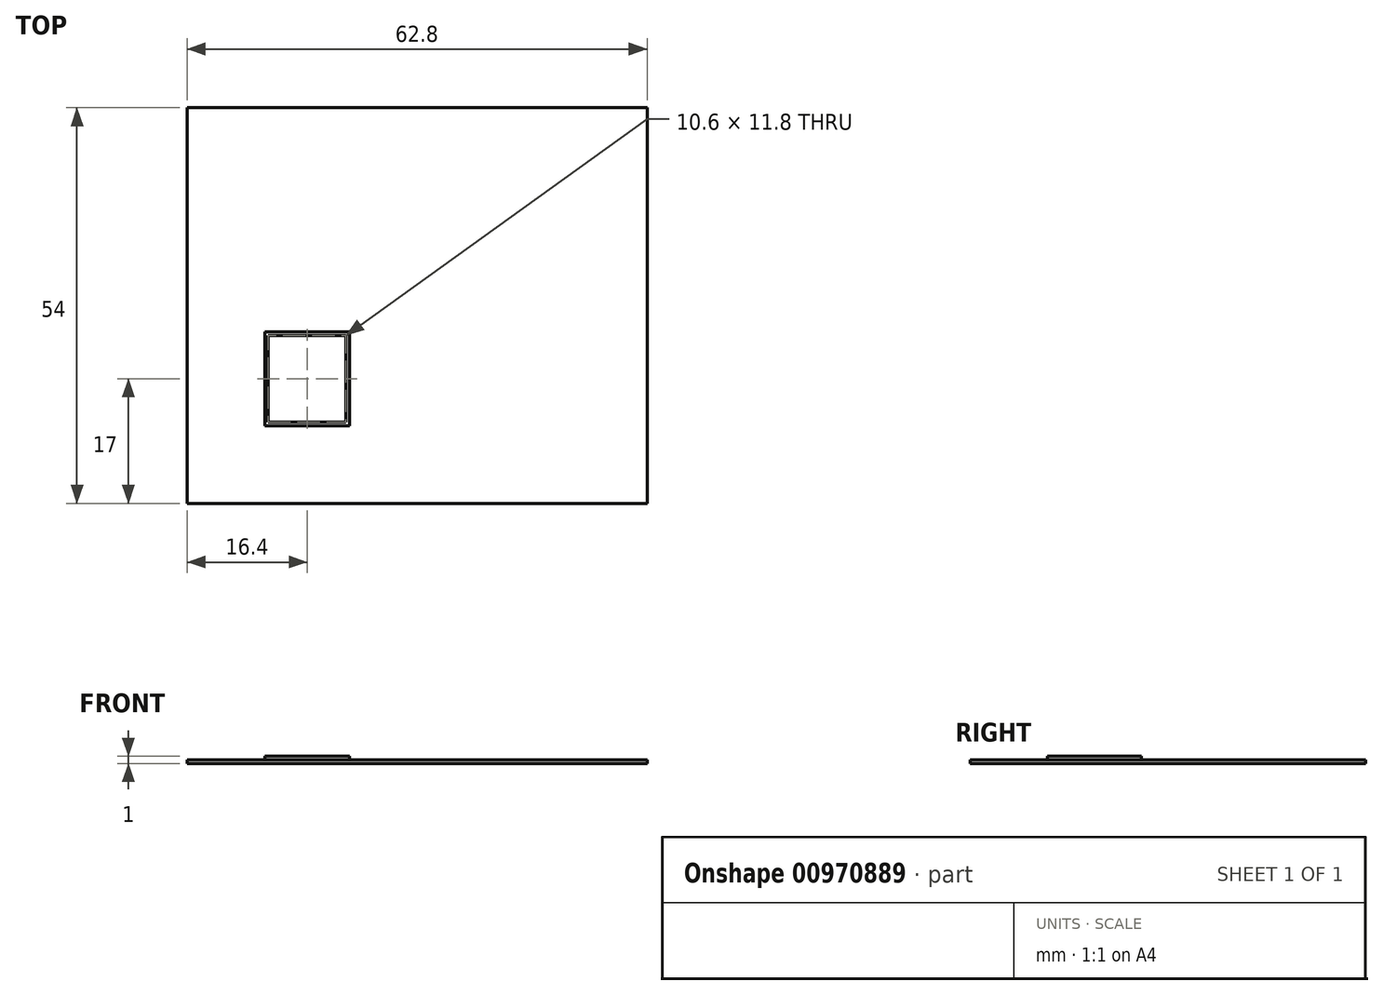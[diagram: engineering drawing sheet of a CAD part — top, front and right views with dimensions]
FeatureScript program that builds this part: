
annotation { "Feature Type Name" : "Feature", "Feature Type Description" : "" }
export const myFeature = defineFeature(function(context is Context, id is Id, definition is map)
    precondition{}
    {
        {
            var Q0;
            Q0=qCreatedBy(makeId("Top.planeOp"),FACE);
            var sketch = newSketch(context, id + "F0", { "sketchPlane" : qUnion([Q0])});
            skLineSegment(sketch, "E0.bottom", {"start": v(46.4, 37) * mm, "end": v(-16.4, 37) * mm});
            skLineSegment(sketch, "E0.top", {"start": v(46.4, -17) * mm, "end": v(-16.4, -17) * mm});
            skLineSegment(sketch, "E0.left", {"start": v(46.4, 37) * mm, "end": v(46.4, -17) * mm});
            skLineSegment(sketch, "E0.right", {"start": v(-16.4, 37) * mm, "end": v(-16.4, -17) * mm});
            skPoint(sketch, "E0.middle", {"position": v(0, 0) * mm});
            skLineSegment(sketch, "E1.bottom", {"start": v(6.4, 7) * mm, "end": v(-6.4, 7) * mm});
            skLineSegment(sketch, "E1.top", {"start": v(6.4, -7) * mm, "end": v(-6.4, -7) * mm});
            skLineSegment(sketch, "E1.left", {"start": v(6.4, 7) * mm, "end": v(6.4, -7) * mm});
            skLineSegment(sketch, "E1.right", {"start": v(-6.4, 7) * mm, "end": v(-6.4, -7) * mm});
            skLineSegment(sketch, "E2.0", {"start": v(5.8, 6.4) * mm, "end": v(5.8, -6.4) * mm});
            skLineSegment(sketch, "E2.1", {"start": v(5.8, 6.4) * mm, "end": v(-5.8, 6.4) * mm});
            skLineSegment(sketch, "E2.2", {"start": v(-5.8, 6.4) * mm, "end": v(-5.8, -6.4) * mm});
            skLineSegment(sketch, "E2.3", {"start": v(5.8, -6.4) * mm, "end": v(-5.8, -6.4) * mm});
            skLineSegment(sketch, "E3.0", {"start": v(5.3, 5.9) * mm, "end": v(5.3, -5.9) * mm});
            skLineSegment(sketch, "E3.1", {"start": v(5.3, 5.9) * mm, "end": v(-5.3, 5.9) * mm});
            skLineSegment(sketch, "E3.2", {"start": v(-5.3, 5.9) * mm, "end": v(-5.3, -5.9) * mm});
            skLineSegment(sketch, "E3.3", {"start": v(5.3, -5.9) * mm, "end": v(-5.3, -5.9) * mm});
            skSolve(sketch);
        }
        {
            var Q0;
            Q0=makeQuery(id+"F0.imprint","IMPRINT",FACE,{"disambiguationData":[TD([[makeQuery(id+"F0.imprint","IMPRINT",EDGE,{"derivedFrom":sQuery(id+"F0.wireOp",EDGE,"E0.bottom")}),1.0]])]});
            var Q1;
            Q1=makeQuery(id+"F0.imprint","IMPRINT",FACE,{"disambiguationData":[TD([[makeQuery(id+"F0.imprint","IMPRINT",EDGE,{"derivedFrom":sQuery(id+"F0.wireOp",EDGE,"E1.bottom")}),1.0]])]});
            var Q2;
            Q2=makeQuery(id+"F0.imprint","IMPRINT",FACE,{"disambiguationData":[TD([[makeQuery(id+"F0.imprint","IMPRINT",EDGE,{"derivedFrom":sQuery(id+"F0.wireOp",EDGE,"E2.0")}),-1.0]])]});
            extrude(context, id + "F1", {"entities" : qUnion([Q0, Q1, Q2]), "depth" : 0.5 * mm, "offsetDistance" : 25 * mm});
        }
        {
            var Q0;
            Q0=makeQuery(id+"F0.imprint","IMPRINT",FACE,{"disambiguationData":[TD([[makeQuery(id+"F0.imprint","IMPRINT",EDGE,{"derivedFrom":sQuery(id+"F0.wireOp",EDGE,"E2.0")}),-1.0]])]});
            extrude(context, id + "F2", {"entities" : qUnion([Q0]), "operationType" : NewBodyOperationType.ADD, "depth" : 1 * mm, "offsetDistance" : 25 * mm});
        }
    });
